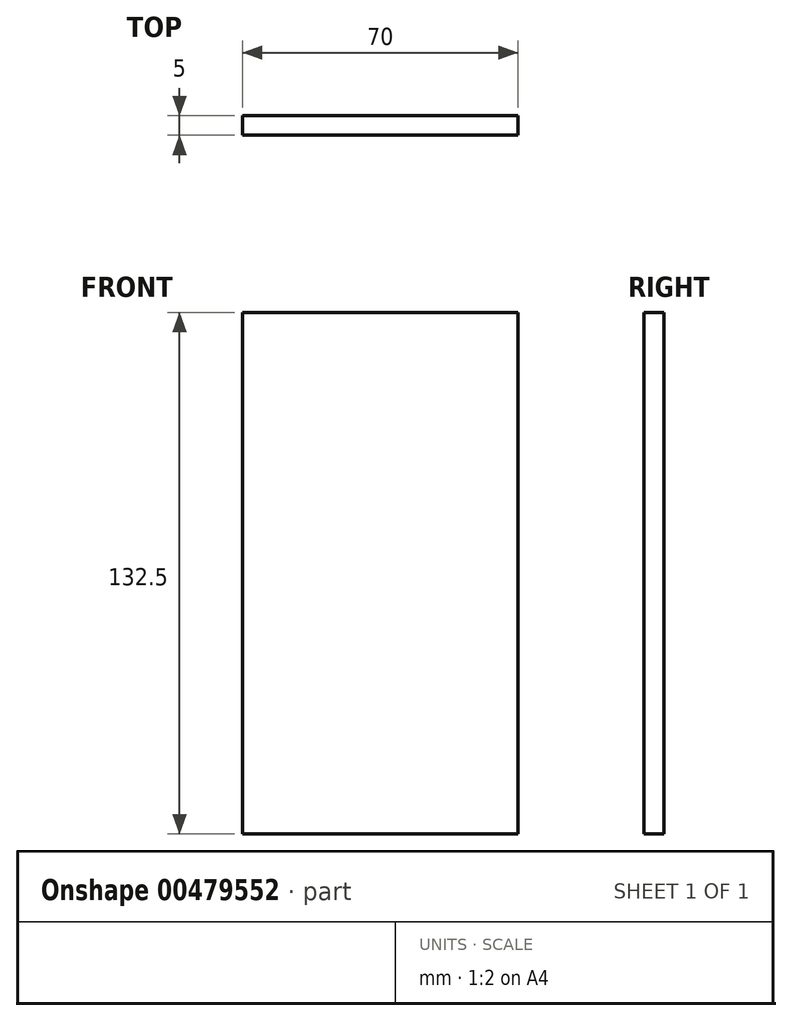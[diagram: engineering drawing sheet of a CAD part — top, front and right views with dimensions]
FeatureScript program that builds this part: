
annotation { "Feature Type Name" : "Feature", "Feature Type Description" : "" }
export const myFeature = defineFeature(function(context is Context, id is Id, definition is map)
    precondition{}
    {
        {
            var Q0;
            Q0=qCreatedBy(makeId("Right.planeOp"),FACE);
            var sketch = newSketch(context, id + "F0", { "sketchPlane" : qUnion([Q0])});
            skLineSegment(sketch, "E0", {"start": v(-2.5, 0) * mm, "end": v(2.5, 0) * mm});
            skPoint(sketch, "E1.visualSharp", {"position": v(2.5, 132.5) * mm});
            skLineSegment(sketch, "E2", {"start": v(2.5, 0) * mm, "end": v(2.5, 132.5) * mm});
            skLineSegment(sketch, "E3", {"start": v(2.5, 132.5) * mm, "end": v(-2.5, 132.5) * mm});
            skLineSegment(sketch, "E4", {"start": v(-2.5, 0) * mm, "end": v(-2.5, 132.5) * mm});
            skSolve(sketch);
        }
        {
            var Q0;
            Q0 = qSketchRegion(id + "F0", true);
            extrude(context, id + "F1", {"entities" : qUnion([Q0]), "depth" : 70 * mm});
        }
    });
